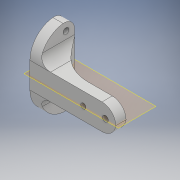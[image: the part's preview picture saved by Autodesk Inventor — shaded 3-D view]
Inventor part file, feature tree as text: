
AUTODESK INVENTOR PART (.ipt)
format: ipt  version: 2018.2 (Build 222227000, 227)  size: 237,056 bytes
history: native  units: mm
features: sketch x11, extrude x10, fillet x10, mirror x4, hole x2, plane x2, projected_geometry x1
ambient origin geometry x8: Origin, YZ Plane, XZ Plane, XY Plane, X Axis, Y Axis, Z Axis, Center Point
bodies: Solid1 (feature_tree)
feature tree (40):
  extrude  "Extrusion1"  Depth=20.0mm
  hole  "Hole1"  [1 undecoded]
  fillet  "Fillet1"  Radius=24.0mm
  fillet  "Fillet2"  Radius=18.0mm
  hole  "Hole2"  [1 undecoded]
  sketch  "Sketch5"  dims[d17=3.0mm d18=6.0mm d19=4.0mm d20=2.0mm d21=90.0deg d22=8.0mm d23=20.594885mm d29=8.0mm d30=10.0mm d31=0.0mm]
  fillet  "Fillet4"  Radius=10.0mm
  extrude  "Extrusion3"  Depth=10.0mm
  plane  "Work Plane1"
  extrude  "Extrusion4"  Depth=6.0mm
  fillet  "Fillet7"  Radius=3.3528mm
  fillet  "Fillet8"  Radius=10.0mm
  sketch  "Sketch7"  dims[d41=6.0mm d42=6.0mm d44=3.3528mm d45=10.0mm d46=0.0mm]
  extrude  "Extrusion5"  Depth=10.0mm TaperAngle=0.0deg
  extrude  "Extrusion6"  Depth=10.0mm TaperAngle=0.0deg
  extrude  "Extrusion7"  Depth=3.3528mm
  extrude  "Extrusion8"  Depth=6.0mm
  fillet  "Fillet10"  Radius=6.0mm
  fillet  "Fillet11"  Radius=10.0mm
  plane  "Work Plane2"
  extrude  "Extrusion9"  Depth=15.0mm
  extrude  "Extrusion10"  Depth=6.0mm
  fillet  "Fillet12"  Radius=5.0mm
  extrude  "Extrusion11"  Depth=15.0mm TaperAngle=0.0deg
  fillet  "Fillet13"  Radius=6.0mm
  mirror  "Mirror1"
  mirror  "Mirror2"
  mirror  "Mirror3"
  mirror  "Mirror4"
  fillet  "Fillet14"  Radius=6.0mm
  sketch  "Sketch1"  dims[d0=20.0mm d1=50.0mm]
  sketch  "Sketch2"  dims[d2=6.0mm d3=15.0mm d4=0.0mm]
  sketch  "Sketch3"  dims[d8=3.4036mm d9=6.0mm d10=4.0mm d11=2.0mm d12=90.0deg d13=8.0mm d14=20.594885mm d15=24.0mm d16=18.0mm]
  sketch  "Sketch6"  dims[d35=10.0mm d36=0.0mm d39=10.0mm]
  projected_geometry  "Projected Loop1"
  sketch  "Sketch8"  dims[d47=10.0mm d48=0.0mm d49=10.0mm d50=0.0mm]
  sketch  "Sketch9"  dims[d51=8.0mm d52=10.0mm d53=0.0mm]
  sketch  "Sketch14"  dims[d54=3.3528mm d55=3.3528mm]
  sketch  "Sketch15"  dims[d56=10.0mm d57=6.0mm d58=6.0mm d59=10.0mm d60=0.0mm]
  sketch  "Sketch16"  dims[d61=15.0mm d62=0.0mm d63=15.0mm d64=3.4036mm d65=5.0mm d66=15.0mm d67=0.0mm d68=6.0mm d69=6.0mm]
note: 2 required parameter values undecoded (feature->parameter linkage not recoverable at this tier; creation-order binding heuristic only, values carry confidence <= 0.55)
